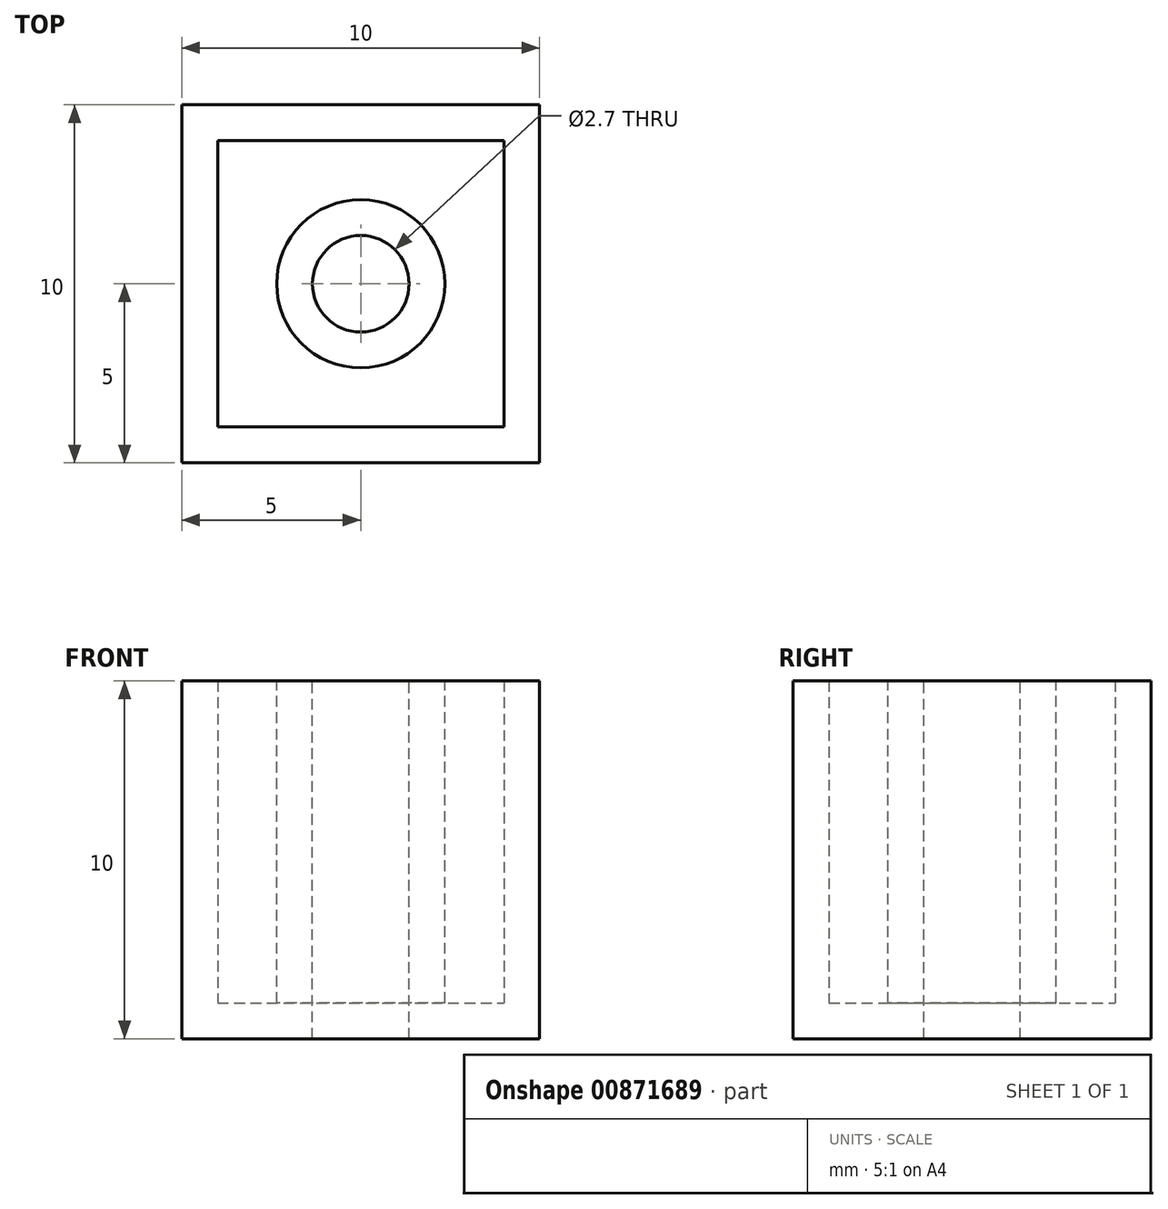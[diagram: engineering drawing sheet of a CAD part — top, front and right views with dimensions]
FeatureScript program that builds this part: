
annotation { "Feature Type Name" : "Feature", "Feature Type Description" : "" }
export const myFeature = defineFeature(function(context is Context, id is Id, definition is map)
    precondition{}
    {
        {
            var Q0;
            Q0=qCreatedBy(makeId("Top.planeOp"),FACE);
            var sketch = newSketch(context, id + "F0", { "sketchPlane" : qUnion([Q0])});
            skLineSegment(sketch, "E0.bottom", {"start": v(0, 0) * mm, "end": v(10, 0) * mm});
            skLineSegment(sketch, "E0.top", {"start": v(0, 10) * mm, "end": v(10, 10) * mm});
            skLineSegment(sketch, "E0.left", {"start": v(0, 0) * mm, "end": v(0, 10) * mm});
            skLineSegment(sketch, "E0.right", {"start": v(10, 0) * mm, "end": v(10, 10) * mm});
            skSolve(sketch);
        }
        {
            var Q0;
            Q0=makeQuery(id+"F0.imprint","IMPRINT",FACE,{"disambiguationData":[TD([[makeQuery(id+"F0.imprint","IMPRINT",EDGE,{"derivedFrom":sQuery(id+"F0.wireOp",EDGE,"E0.bottom")}),1.0]])]});
            extrude(context, id + "F1", {"entities" : qUnion([Q0]), "depth" : 10 * mm, "offsetDistance" : 25 * mm});
        }
        {
            var Q0;
            Q0=makeQuery(id+"F1.opExtrude","CAP_FACE",FACE,{"disambiguationData":[OSD([sQuery(id+"F0.wireOp",EDGE,"E0.bottom"),sQuery(id+"F0.wireOp",EDGE,"E0.top"),sQuery(id+"F0.wireOp",EDGE,"E0.left"),sQuery(id+"F0.wireOp",EDGE,"E0.right")])],"isStart":false});
            var sketch = newSketch(context, id + "F2", { "sketchPlane" : qUnion([Q0])});
            skLineSegment(sketch, "E1", {"start": v(0, 10) * mm, "end": v(10, 0) * mm});
            skPoint(sketch, "E2", {"position": v(5, 5) * mm});
            skSolve(sketch);
        }
        {
            var Q0;
            Q0=sQuery(id+"F2.wireOp",VERTEX,"E2");
            var Q1;
            Q1=makeQuery(id+"F1.opExtrude","SWEPT_BODY",BODY,{"disambiguationData":[OSD([sQuery(id+"F0.wireOp",EDGE,"E0.bottom"),sQuery(id+"F0.wireOp",EDGE,"E0.top"),sQuery(id+"F0.wireOp",EDGE,"E0.left"),sQuery(id+"F0.wireOp",EDGE,"E0.right")])]});
            hole(context, id + "F3", {"style" : HoleStyle.SIMPLE, "endStyle" : HoleEndStyle.THROUGH, "standardTappedOrClearance" : lookupTablePath({ "standard" : "ISO", "engagement" : "50%", "pitch" : "0.5 mm", "size" : "M3", "type" : "Tapped" }), "standardBlindInLast" : lookupTablePath({ "standard" : "ISO", "engagement" : "50%", "pitch" : "0.5 mm", "size" : "M3", "type" : "Tapped" }), "holeDiameter" : 2.7 * mm, "majorDiameter" : 3 * mm, "showTappedDepth" : true, "isTappedThrough" : true, "tappedDepth" : 12 * mm, "tapClearance" : 3, "locations" : qUnion([Q0]), "scope" : qUnion([Q1])});
        }
        {
            var Q0;
            Q0=makeQuery(id+"F1.opExtrude","CAP_FACE",FACE,{"disambiguationData":[OSD([sQuery(id+"F0.wireOp",EDGE,"E0.bottom"),sQuery(id+"F0.wireOp",EDGE,"E0.top"),sQuery(id+"F0.wireOp",EDGE,"E0.left"),sQuery(id+"F0.wireOp",EDGE,"E0.right")])],"isStart":false});
            shell(context, id + "F4", {"entities" : qUnion([Q0]), "thickness" : 1 * mm});
        }
    });
